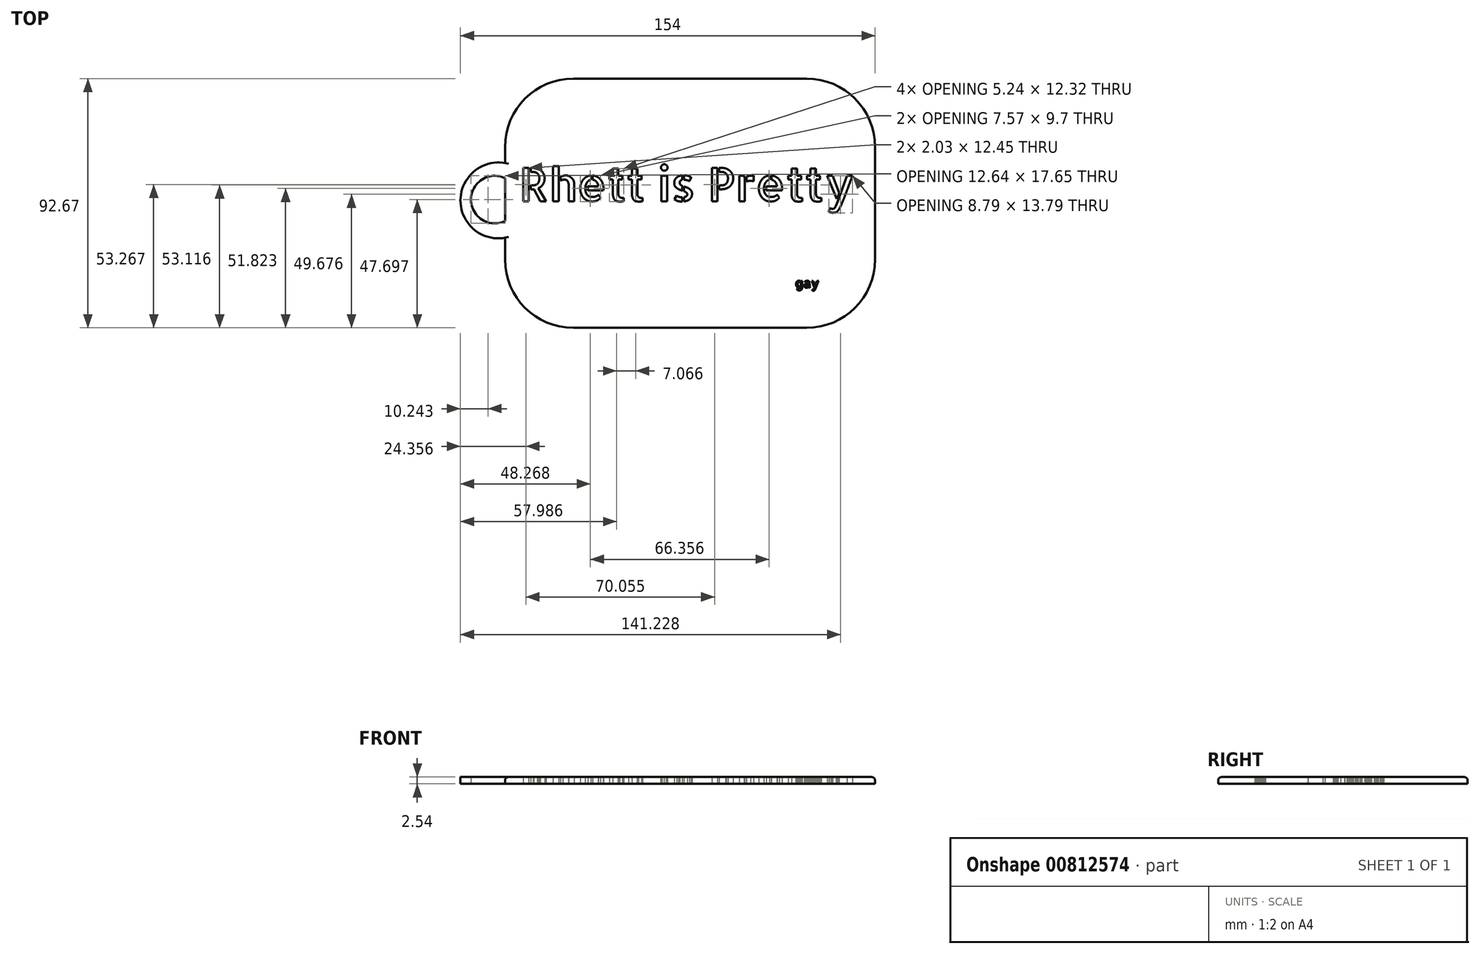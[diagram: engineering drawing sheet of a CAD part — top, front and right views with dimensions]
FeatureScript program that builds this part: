
annotation { "Feature Type Name" : "Feature", "Feature Type Description" : "" }
export const myFeature = defineFeature(function(context is Context, id is Id, definition is map)
    precondition{}
    {
        {
            var Q0;
            Q0=qCreatedBy(makeId("Top.planeOp"),FACE);
            var sketch = newSketch(context, id + "F0", { "sketchPlane" : qUnion([Q0])});
            skLineSegment(sketch, "E0.bottom", {"start": v(-64.83, 43.87) * mm, "end": v(72.61, 43.87) * mm});
            skLineSegment(sketch, "E0.top", {"start": v(-64.83, -48.8) * mm, "end": v(72.61, -48.8) * mm});
            skLineSegment(sketch, "E0.left", {"start": v(-64.83, 43.87) * mm, "end": v(-64.83, 12.46) * mm});
            skLineSegment(sketch, "E0.right", {"start": v(72.61, 43.87) * mm, "end": v(72.61, -48.8) * mm});
            skText(sketch, "E1", { "text": "Rhett is Pretty", "fontName": "AllertaStencil-Regular.ttf"});
            skText(sketch, "E2", { "text": "gay", "fontName": "AllertaStencil-Regular.ttf"});
            skArc(sketch, "E3", {"start": v(-64.83, 12.46) * mm, "mid": v(-81.4, -1.43) * mm, "end": v(-64.83, -15.31) * mm});
            skArc(sketch, "E4", {"start": v(-64.83, 6.88) * mm, "mid": v(-77.47, -1.1) * mm, "end": v(-64.83, -9.08) * mm});
            skLineSegment(sketch, "E5.trimOffspring", {"start": v(-64.83, -15.31) * mm, "end": v(-64.83, -48.8) * mm});
            skLineSegment(sketch, "E6", {"start": v(-64.83, 6.88) * mm, "end": v(-64.83, -9.08) * mm});
            const initialGuessF0  = {"E1": [-0.05957, -0.00176, 1, 0, 0.01246], "E2": [0.04298, -0.03385, 1, 0, 0.00333]};
            skSetInitialGuess(sketch, initialGuessF0);
            skSolve(sketch);
        }
        {
            var Q0;
            Q0=makeQuery(id+"F0.imprint","IMPRINT",FACE,{"disambiguationData":[TD([[makeQuery(id+"F0.imprint","IMPRINT",EDGE,{"derivedFrom":sQuery(id+"F0.wireOp",EDGE,"E0.bottom")}),-1.0]])]});
            extrude(context, id + "F1", {"entities" : qUnion([Q0]), "depth" : 2.54 * mm, "offsetDistance" : 25.4 * mm});
        }
        {
            var Q0;
            Q0=makeQuery(id+"F1.opExtrude","SWEPT_EDGE",EDGE,{"disambiguationData":[OSD([sQuery(id+"F0.wireOp",EDGE,"E0.bottom"),sQuery(id+"F0.wireOp",EDGE,"E0.left")])]});
            var Q1;
            Q1=makeQuery(id+"F1.opExtrude","SWEPT_EDGE",EDGE,{"disambiguationData":[OSD([sQuery(id+"F0.wireOp",EDGE,"E0.bottom"),sQuery(id+"F0.wireOp",EDGE,"E0.right")])]});
            var Q2;
            Q2=makeQuery(id+"F1.opExtrude","SWEPT_EDGE",EDGE,{"disambiguationData":[OSD([sQuery(id+"F0.wireOp",EDGE,"E0.top"),sQuery(id+"F0.wireOp",EDGE,"E0.right")])]});
            var Q3;
            Q3=makeQuery(id+"F1.opExtrude","SWEPT_EDGE",EDGE,{"disambiguationData":[OSD([sQuery(id+"F0.wireOp",EDGE,"E0.top"),sQuery(id+"F0.wireOp",EDGE,"E5.trimOffspring")])]});
            fillet(context, id + "F2", {"entities" : qUnion([Q0, Q1, Q2, Q3]), "radius" : 25.4 * mm, "tangentPropagation" : true, "allowEdgeOverflow" : false});
        }
        {
            var Q0;
            {var subQ0=sQuery(id+"F0.wireOp",EDGE,"E5.trimOffspring");var subQ1=sQuery(id+"F0.wireOp",EDGE,"E0.top");Q0=makeQuery(id+"F2.opFillet","BLEND_EDGE",EDGE,{"blendedFrom":[makeQuery(id+"F1.opExtrude","SWEPT_EDGE",EDGE,{"disambiguationData":[OSD([subQ1,subQ0])]}),makeQuery(id+"F1.opExtrude","CAP_FACE",FACE,{"disambiguationData":[OSD([sQuery(id+"F0.wireOp",EDGE,"E0.bottom"),subQ1,sQuery(id+"F0.wireOp",EDGE,"E0.left"),sQuery(id+"F0.wireOp",EDGE,"E0.right"),sQuery(id+"F0.wireOp",EDGE,"E1.sketch_text.stroke-0"),sQuery(id+"F0.wireOp",EDGE,"E1.sketch_text.stroke-1"),sQuery(id+"F0.wireOp",EDGE,"E1.sketch_text.stroke-2"),sQuery(id+"F0.wireOp",EDGE,"E1.sketch_text.stroke-3"),sQuery(id+"F0.wireOp",EDGE,"E1.sketch_text.stroke-4"),sQuery(id+"F0.wireOp",EDGE,"E1.sketch_text.stroke-5"),sQuery(id+"F0.wireOp",EDGE,"E1.sketch_text.stroke-6"),sQuery(id+"F0.wireOp",EDGE,"E1.sketch_text.stroke-7"),sQuery(id+"F0.wireOp",EDGE,"E1.sketch_text.stroke-8"),sQuery(id+"F0.wireOp",EDGE,"E1.sketch_text.stroke-9"),sQuery(id+"F0.wireOp",EDGE,"E1.sketch_text.stroke-10"),sQuery(id+"F0.wireOp",EDGE,"E1.sketch_text.stroke-11"),sQuery(id+"F0.wireOp",EDGE,"E1.sketch_text.stroke-12"),sQuery(id+"F0.wireOp",EDGE,"E1.sketch_text.stroke-13"),sQuery(id+"F0.wireOp",EDGE,"E1.sketch_text.stroke-14"),sQuery(id+"F0.wireOp",EDGE,"E1.sketch_text.stroke-15"),sQuery(id+"F0.wireOp",EDGE,"E1.sketch_text.stroke-16"),sQuery(id+"F0.wireOp",EDGE,"E1.sketch_text.stroke-17"),sQuery(id+"F0.wireOp",EDGE,"E1.sketch_text.stroke-18"),sQuery(id+"F0.wireOp",EDGE,"E1.sketch_text.stroke-19"),sQuery(id+"F0.wireOp",EDGE,"E1.sketch_text.stroke-20"),sQuery(id+"F0.wireOp",EDGE,"E1.sketch_text.stroke-21"),sQuery(id+"F0.wireOp",EDGE,"E1.sketch_text.stroke-22"),sQuery(id+"F0.wireOp",EDGE,"E1.sketch_text.stroke-23"),sQuery(id+"F0.wireOp",EDGE,"E1.sketch_text.stroke-24"),sQuery(id+"F0.wireOp",EDGE,"E1.sketch_text.stroke-25"),sQuery(id+"F0.wireOp",EDGE,"E1.sketch_text.stroke-26"),sQuery(id+"F0.wireOp",EDGE,"E1.sketch_text.stroke-27"),sQuery(id+"F0.wireOp",EDGE,"E1.sketch_text.stroke-28"),sQuery(id+"F0.wireOp",EDGE,"E1.sketch_text.stroke-29"),sQuery(id+"F0.wireOp",EDGE,"E1.sketch_text.stroke-30"),sQuery(id+"F0.wireOp",EDGE,"E1.sketch_text.stroke-31"),sQuery(id+"F0.wireOp",EDGE,"E1.sketch_text.stroke-32"),sQuery(id+"F0.wireOp",EDGE,"E1.sketch_text.stroke-33"),sQuery(id+"F0.wireOp",EDGE,"E1.sketch_text.stroke-34"),sQuery(id+"F0.wireOp",EDGE,"E1.sketch_text.stroke-35"),sQuery(id+"F0.wireOp",EDGE,"E1.sketch_text.stroke-36"),sQuery(id+"F0.wireOp",EDGE,"E1.sketch_text.stroke-37"),sQuery(id+"F0.wireOp",EDGE,"E1.sketch_text.stroke-38"),sQuery(id+"F0.wireOp",EDGE,"E1.sketch_text.stroke-39"),sQuery(id+"F0.wireOp",EDGE,"E1.sketch_text.stroke-40"),sQuery(id+"F0.wireOp",EDGE,"E1.sketch_text.stroke-41"),sQuery(id+"F0.wireOp",EDGE,"E1.sketch_text.stroke-42"),sQuery(id+"F0.wireOp",EDGE,"E1.sketch_text.stroke-43"),sQuery(id+"F0.wireOp",EDGE,"E1.sketch_text.stroke-44"),sQuery(id+"F0.wireOp",EDGE,"E1.sketch_text.stroke-45"),sQuery(id+"F0.wireOp",EDGE,"E1.sketch_text.stroke-46"),sQuery(id+"F0.wireOp",EDGE,"E1.sketch_text.stroke-47"),sQuery(id+"F0.wireOp",EDGE,"E1.sketch_text.stroke-48"),sQuery(id+"F0.wireOp",EDGE,"E1.sketch_text.stroke-49"),sQuery(id+"F0.wireOp",EDGE,"E1.sketch_text.stroke-50"),sQuery(id+"F0.wireOp",EDGE,"E1.sketch_text.stroke-51"),sQuery(id+"F0.wireOp",EDGE,"E1.sketch_text.stroke-52"),sQuery(id+"F0.wireOp",EDGE,"E1.sketch_text.stroke-53"),sQuery(id+"F0.wireOp",EDGE,"E1.sketch_text.stroke-54"),sQuery(id+"F0.wireOp",EDGE,"E1.sketch_text.stroke-55"),sQuery(id+"F0.wireOp",EDGE,"E1.sketch_text.stroke-56"),sQuery(id+"F0.wireOp",EDGE,"E1.sketch_text.stroke-57"),sQuery(id+"F0.wireOp",EDGE,"E1.sketch_text.stroke-58"),sQuery(id+"F0.wireOp",EDGE,"E1.sketch_text.stroke-59"),sQuery(id+"F0.wireOp",EDGE,"E1.sketch_text.stroke-60"),sQuery(id+"F0.wireOp",EDGE,"E1.sketch_text.stroke-61"),sQuery(id+"F0.wireOp",EDGE,"E1.sketch_text.stroke-62"),sQuery(id+"F0.wireOp",EDGE,"E1.sketch_text.stroke-63"),sQuery(id+"F0.wireOp",EDGE,"E1.sketch_text.stroke-64"),sQuery(id+"F0.wireOp",EDGE,"E1.sketch_text.stroke-65"),sQuery(id+"F0.wireOp",EDGE,"E1.sketch_text.stroke-66"),sQuery(id+"F0.wireOp",EDGE,"E1.sketch_text.stroke-67"),sQuery(id+"F0.wireOp",EDGE,"E1.sketch_text.stroke-68"),sQuery(id+"F0.wireOp",EDGE,"E1.sketch_text.stroke-69"),sQuery(id+"F0.wireOp",EDGE,"E1.sketch_text.stroke-70"),sQuery(id+"F0.wireOp",EDGE,"E1.sketch_text.stroke-71"),sQuery(id+"F0.wireOp",EDGE,"E1.sketch_text.stroke-72"),sQuery(id+"F0.wireOp",EDGE,"E1.sketch_text.stroke-73"),sQuery(id+"F0.wireOp",EDGE,"E1.sketch_text.stroke-74"),sQuery(id+"F0.wireOp",EDGE,"E1.sketch_text.stroke-75"),sQuery(id+"F0.wireOp",EDGE,"E1.sketch_text.stroke-76"),sQuery(id+"F0.wireOp",EDGE,"E1.sketch_text.stroke-77"),sQuery(id+"F0.wireOp",EDGE,"E1.sketch_text.stroke-78"),sQuery(id+"F0.wireOp",EDGE,"E1.sketch_text.stroke-79"),sQuery(id+"F0.wireOp",EDGE,"E1.sketch_text.stroke-80"),sQuery(id+"F0.wireOp",EDGE,"E1.sketch_text.stroke-81"),sQuery(id+"F0.wireOp",EDGE,"E1.sketch_text.stroke-82"),sQuery(id+"F0.wireOp",EDGE,"E1.sketch_text.stroke-83"),sQuery(id+"F0.wireOp",EDGE,"E1.sketch_text.stroke-84"),sQuery(id+"F0.wireOp",EDGE,"E1.sketch_text.stroke-85"),sQuery(id+"F0.wireOp",EDGE,"E1.sketch_text.stroke-86"),sQuery(id+"F0.wireOp",EDGE,"E1.sketch_text.stroke-87"),sQuery(id+"F0.wireOp",EDGE,"E1.sketch_text.stroke-88"),sQuery(id+"F0.wireOp",EDGE,"E1.sketch_text.stroke-89"),sQuery(id+"F0.wireOp",EDGE,"E1.sketch_text.stroke-90"),sQuery(id+"F0.wireOp",EDGE,"E1.sketch_text.stroke-91"),sQuery(id+"F0.wireOp",EDGE,"E1.sketch_text.stroke-92"),sQuery(id+"F0.wireOp",EDGE,"E1.sketch_text.stroke-93"),sQuery(id+"F0.wireOp",EDGE,"E1.sketch_text.stroke-94"),sQuery(id+"F0.wireOp",EDGE,"E1.sketch_text.stroke-95"),sQuery(id+"F0.wireOp",EDGE,"E1.sketch_text.stroke-96"),sQuery(id+"F0.wireOp",EDGE,"E1.sketch_text.stroke-97"),sQuery(id+"F0.wireOp",EDGE,"E1.sketch_text.stroke-98"),sQuery(id+"F0.wireOp",EDGE,"E1.sketch_text.stroke-99"),sQuery(id+"F0.wireOp",EDGE,"E1.sketch_text.stroke-100"),sQuery(id+"F0.wireOp",EDGE,"E1.sketch_text.stroke-101"),sQuery(id+"F0.wireOp",EDGE,"E1.sketch_text.stroke-102"),sQuery(id+"F0.wireOp",EDGE,"E1.sketch_text.stroke-103"),sQuery(id+"F0.wireOp",EDGE,"E1.sketch_text.stroke-104"),sQuery(id+"F0.wireOp",EDGE,"E1.sketch_text.stroke-105"),sQuery(id+"F0.wireOp",EDGE,"E1.sketch_text.stroke-106"),sQuery(id+"F0.wireOp",EDGE,"E1.sketch_text.stroke-107"),sQuery(id+"F0.wireOp",EDGE,"E1.sketch_text.stroke-108"),sQuery(id+"F0.wireOp",EDGE,"E1.sketch_text.stroke-109"),sQuery(id+"F0.wireOp",EDGE,"E1.sketch_text.stroke-110"),sQuery(id+"F0.wireOp",EDGE,"E1.sketch_text.stroke-111"),sQuery(id+"F0.wireOp",EDGE,"E1.sketch_text.stroke-112"),sQuery(id+"F0.wireOp",EDGE,"E1.sketch_text.stroke-113"),sQuery(id+"F0.wireOp",EDGE,"E1.sketch_text.stroke-114"),sQuery(id+"F0.wireOp",EDGE,"E1.sketch_text.stroke-115"),sQuery(id+"F0.wireOp",EDGE,"E1.sketch_text.stroke-116"),sQuery(id+"F0.wireOp",EDGE,"E1.sketch_text.stroke-117"),sQuery(id+"F0.wireOp",EDGE,"E1.sketch_text.stroke-118"),sQuery(id+"F0.wireOp",EDGE,"E1.sketch_text.stroke-119"),sQuery(id+"F0.wireOp",EDGE,"E1.sketch_text.stroke-120"),sQuery(id+"F0.wireOp",EDGE,"E1.sketch_text.stroke-121"),sQuery(id+"F0.wireOp",EDGE,"E1.sketch_text.stroke-122"),sQuery(id+"F0.wireOp",EDGE,"E1.sketch_text.stroke-123"),sQuery(id+"F0.wireOp",EDGE,"E1.sketch_text.stroke-124"),sQuery(id+"F0.wireOp",EDGE,"E1.sketch_text.stroke-125"),sQuery(id+"F0.wireOp",EDGE,"E1.sketch_text.stroke-126"),sQuery(id+"F0.wireOp",EDGE,"E1.sketch_text.stroke-127"),sQuery(id+"F0.wireOp",EDGE,"E1.sketch_text.stroke-128"),sQuery(id+"F0.wireOp",EDGE,"E1.sketch_text.stroke-129"),sQuery(id+"F0.wireOp",EDGE,"E1.sketch_text.stroke-130"),sQuery(id+"F0.wireOp",EDGE,"E1.sketch_text.stroke-131"),sQuery(id+"F0.wireOp",EDGE,"E1.sketch_text.stroke-132"),sQuery(id+"F0.wireOp",EDGE,"E1.sketch_text.stroke-133"),sQuery(id+"F0.wireOp",EDGE,"E1.sketch_text.stroke-134"),sQuery(id+"F0.wireOp",EDGE,"E1.sketch_text.stroke-135"),sQuery(id+"F0.wireOp",EDGE,"E1.sketch_text.stroke-136"),sQuery(id+"F0.wireOp",EDGE,"E1.sketch_text.stroke-137"),sQuery(id+"F0.wireOp",EDGE,"E1.sketch_text.stroke-138"),sQuery(id+"F0.wireOp",EDGE,"E1.sketch_text.stroke-139"),sQuery(id+"F0.wireOp",EDGE,"E1.sketch_text.stroke-140"),sQuery(id+"F0.wireOp",EDGE,"E1.sketch_text.stroke-141"),sQuery(id+"F0.wireOp",EDGE,"E1.sketch_text.stroke-142"),sQuery(id+"F0.wireOp",EDGE,"E1.sketch_text.stroke-143"),sQuery(id+"F0.wireOp",EDGE,"E1.sketch_text.stroke-144"),sQuery(id+"F0.wireOp",EDGE,"E1.sketch_text.stroke-145"),sQuery(id+"F0.wireOp",EDGE,"E1.sketch_text.stroke-146"),sQuery(id+"F0.wireOp",EDGE,"E1.sketch_text.stroke-147"),sQuery(id+"F0.wireOp",EDGE,"E1.sketch_text.stroke-148"),sQuery(id+"F0.wireOp",EDGE,"E1.sketch_text.stroke-149"),sQuery(id+"F0.wireOp",EDGE,"E1.sketch_text.stroke-150"),sQuery(id+"F0.wireOp",EDGE,"E1.sketch_text.stroke-151"),sQuery(id+"F0.wireOp",EDGE,"E1.sketch_text.stroke-152"),sQuery(id+"F0.wireOp",EDGE,"E1.sketch_text.stroke-153"),sQuery(id+"F0.wireOp",EDGE,"E1.sketch_text.stroke-154"),sQuery(id+"F0.wireOp",EDGE,"E1.sketch_text.stroke-155"),sQuery(id+"F0.wireOp",EDGE,"E1.sketch_text.stroke-156"),sQuery(id+"F0.wireOp",EDGE,"E1.sketch_text.stroke-157"),sQuery(id+"F0.wireOp",EDGE,"E1.sketch_text.stroke-158"),sQuery(id+"F0.wireOp",EDGE,"E1.sketch_text.stroke-159"),sQuery(id+"F0.wireOp",EDGE,"E1.sketch_text.stroke-160"),sQuery(id+"F0.wireOp",EDGE,"E1.sketch_text.stroke-161"),sQuery(id+"F0.wireOp",EDGE,"E1.sketch_text.stroke-162"),sQuery(id+"F0.wireOp",EDGE,"E1.sketch_text.stroke-163"),sQuery(id+"F0.wireOp",EDGE,"E1.sketch_text.stroke-164"),sQuery(id+"F0.wireOp",EDGE,"E1.sketch_text.stroke-165"),sQuery(id+"F0.wireOp",EDGE,"E1.sketch_text.stroke-166"),sQuery(id+"F0.wireOp",EDGE,"E1.sketch_text.stroke-167"),sQuery(id+"F0.wireOp",EDGE,"E1.sketch_text.stroke-168"),sQuery(id+"F0.wireOp",EDGE,"E1.sketch_text.stroke-169"),sQuery(id+"F0.wireOp",EDGE,"E1.sketch_text.stroke-170"),sQuery(id+"F0.wireOp",EDGE,"E1.sketch_text.stroke-171"),sQuery(id+"F0.wireOp",EDGE,"E1.sketch_text.stroke-172"),sQuery(id+"F0.wireOp",EDGE,"E1.sketch_text.stroke-173"),sQuery(id+"F0.wireOp",EDGE,"E1.sketch_text.stroke-174"),sQuery(id+"F0.wireOp",EDGE,"E1.sketch_text.stroke-175"),sQuery(id+"F0.wireOp",EDGE,"E1.sketch_text.stroke-176"),sQuery(id+"F0.wireOp",EDGE,"E1.sketch_text.stroke-177"),sQuery(id+"F0.wireOp",EDGE,"E1.sketch_text.stroke-178"),sQuery(id+"F0.wireOp",EDGE,"E1.sketch_text.stroke-179"),sQuery(id+"F0.wireOp",EDGE,"E1.sketch_text.stroke-180"),sQuery(id+"F0.wireOp",EDGE,"E1.sketch_text.stroke-181"),sQuery(id+"F0.wireOp",EDGE,"E1.sketch_text.stroke-182"),sQuery(id+"F0.wireOp",EDGE,"E1.sketch_text.stroke-183"),sQuery(id+"F0.wireOp",EDGE,"E1.sketch_text.stroke-184"),sQuery(id+"F0.wireOp",EDGE,"E1.sketch_text.stroke-185"),sQuery(id+"F0.wireOp",EDGE,"E1.sketch_text.stroke-186"),sQuery(id+"F0.wireOp",EDGE,"E1.sketch_text.stroke-187"),sQuery(id+"F0.wireOp",EDGE,"E1.sketch_text.stroke-188"),sQuery(id+"F0.wireOp",EDGE,"E1.sketch_text.stroke-189"),sQuery(id+"F0.wireOp",EDGE,"E1.sketch_text.stroke-190"),sQuery(id+"F0.wireOp",EDGE,"E1.sketch_text.stroke-191"),sQuery(id+"F0.wireOp",EDGE,"E1.sketch_text.stroke-192"),sQuery(id+"F0.wireOp",EDGE,"E1.sketch_text.stroke-193"),sQuery(id+"F0.wireOp",EDGE,"E1.sketch_text.stroke-194"),sQuery(id+"F0.wireOp",EDGE,"E1.sketch_text.stroke-195"),sQuery(id+"F0.wireOp",EDGE,"E1.sketch_text.stroke-196"),sQuery(id+"F0.wireOp",EDGE,"E1.sketch_text.stroke-197"),sQuery(id+"F0.wireOp",EDGE,"E1.sketch_text.stroke-198"),sQuery(id+"F0.wireOp",EDGE,"E1.sketch_text.stroke-199"),sQuery(id+"F0.wireOp",EDGE,"E1.sketch_text.stroke-200"),sQuery(id+"F0.wireOp",EDGE,"E1.sketch_text.stroke-201"),sQuery(id+"F0.wireOp",EDGE,"E1.sketch_text.stroke-202"),sQuery(id+"F0.wireOp",EDGE,"E1.sketch_text.stroke-203"),sQuery(id+"F0.wireOp",EDGE,"E1.sketch_text.stroke-204"),sQuery(id+"F0.wireOp",EDGE,"E1.sketch_text.stroke-205"),sQuery(id+"F0.wireOp",EDGE,"E1.sketch_text.stroke-206"),sQuery(id+"F0.wireOp",EDGE,"E1.sketch_text.stroke-207"),sQuery(id+"F0.wireOp",EDGE,"E1.sketch_text.stroke-208"),sQuery(id+"F0.wireOp",EDGE,"E1.sketch_text.stroke-209"),sQuery(id+"F0.wireOp",EDGE,"E1.sketch_text.stroke-210"),sQuery(id+"F0.wireOp",EDGE,"E1.sketch_text.stroke-211"),sQuery(id+"F0.wireOp",EDGE,"E1.sketch_text.stroke-212"),sQuery(id+"F0.wireOp",EDGE,"E1.sketch_text.stroke-213"),sQuery(id+"F0.wireOp",EDGE,"E1.sketch_text.stroke-214"),sQuery(id+"F0.wireOp",EDGE,"E1.sketch_text.stroke-215"),sQuery(id+"F0.wireOp",EDGE,"E1.sketch_text.stroke-216"),sQuery(id+"F0.wireOp",EDGE,"E1.sketch_text.stroke-217"),sQuery(id+"F0.wireOp",EDGE,"E1.sketch_text.stroke-218"),sQuery(id+"F0.wireOp",EDGE,"E1.sketch_text.stroke-219"),sQuery(id+"F0.wireOp",EDGE,"E1.sketch_text.stroke-220"),sQuery(id+"F0.wireOp",EDGE,"E1.sketch_text.stroke-221"),sQuery(id+"F0.wireOp",EDGE,"E1.sketch_text.stroke-222"),sQuery(id+"F0.wireOp",EDGE,"E1.sketch_text.stroke-223"),sQuery(id+"F0.wireOp",EDGE,"E1.sketch_text.stroke-224"),sQuery(id+"F0.wireOp",EDGE,"E1.sketch_text.stroke-225"),sQuery(id+"F0.wireOp",EDGE,"E1.sketch_text.stroke-226"),sQuery(id+"F0.wireOp",EDGE,"E1.sketch_text.stroke-227"),sQuery(id+"F0.wireOp",EDGE,"E1.sketch_text.stroke-228"),sQuery(id+"F0.wireOp",EDGE,"E1.sketch_text.stroke-229"),sQuery(id+"F0.wireOp",EDGE,"E1.sketch_text.stroke-230"),sQuery(id+"F0.wireOp",EDGE,"E1.sketch_text.stroke-231"),sQuery(id+"F0.wireOp",EDGE,"E1.sketch_text.stroke-232"),sQuery(id+"F0.wireOp",EDGE,"E1.sketch_text.stroke-233"),sQuery(id+"F0.wireOp",EDGE,"E1.sketch_text.stroke-234"),sQuery(id+"F0.wireOp",EDGE,"E1.sketch_text.stroke-235"),sQuery(id+"F0.wireOp",EDGE,"E1.sketch_text.stroke-236"),sQuery(id+"F0.wireOp",EDGE,"E1.sketch_text.stroke-237"),sQuery(id+"F0.wireOp",EDGE,"E1.sketch_text.stroke-238"),sQuery(id+"F0.wireOp",EDGE,"E1.sketch_text.stroke-239"),sQuery(id+"F0.wireOp",EDGE,"E1.sketch_text.stroke-240"),sQuery(id+"F0.wireOp",EDGE,"E1.sketch_text.stroke-241"),sQuery(id+"F0.wireOp",EDGE,"E1.sketch_text.stroke-242"),sQuery(id+"F0.wireOp",EDGE,"E1.sketch_text.stroke-243"),sQuery(id+"F0.wireOp",EDGE,"E1.sketch_text.stroke-244"),sQuery(id+"F0.wireOp",EDGE,"E1.sketch_text.stroke-245"),sQuery(id+"F0.wireOp",EDGE,"E1.sketch_text.stroke-246"),sQuery(id+"F0.wireOp",EDGE,"E1.sketch_text.stroke-247"),sQuery(id+"F0.wireOp",EDGE,"E1.sketch_text.stroke-248"),sQuery(id+"F0.wireOp",EDGE,"E1.sketch_text.stroke-249"),sQuery(id+"F0.wireOp",EDGE,"E1.sketch_text.stroke-250"),sQuery(id+"F0.wireOp",EDGE,"E1.sketch_text.stroke-251"),sQuery(id+"F0.wireOp",EDGE,"E1.sketch_text.stroke-252"),sQuery(id+"F0.wireOp",EDGE,"E1.sketch_text.stroke-253"),sQuery(id+"F0.wireOp",EDGE,"E1.sketch_text.stroke-254"),sQuery(id+"F0.wireOp",EDGE,"E1.sketch_text.stroke-255"),sQuery(id+"F0.wireOp",EDGE,"E1.sketch_text.stroke-256"),sQuery(id+"F0.wireOp",EDGE,"E1.sketch_text.stroke-257"),sQuery(id+"F0.wireOp",EDGE,"E1.sketch_text.stroke-258"),sQuery(id+"F0.wireOp",EDGE,"E1.sketch_text.stroke-259"),sQuery(id+"F0.wireOp",EDGE,"E1.sketch_text.stroke-260"),sQuery(id+"F0.wireOp",EDGE,"E1.sketch_text.stroke-261"),sQuery(id+"F0.wireOp",EDGE,"E1.sketch_text.stroke-262"),sQuery(id+"F0.wireOp",EDGE,"E1.sketch_text.stroke-263"),sQuery(id+"F0.wireOp",EDGE,"E1.sketch_text.stroke-264"),sQuery(id+"F0.wireOp",EDGE,"E1.sketch_text.stroke-265"),sQuery(id+"F0.wireOp",EDGE,"E1.sketch_text.stroke-266"),sQuery(id+"F0.wireOp",EDGE,"E1.sketch_text.stroke-267"),sQuery(id+"F0.wireOp",EDGE,"E1.sketch_text.stroke-268"),sQuery(id+"F0.wireOp",EDGE,"E1.sketch_text.stroke-269"),sQuery(id+"F0.wireOp",EDGE,"E1.sketch_text.stroke-270"),sQuery(id+"F0.wireOp",EDGE,"E1.sketch_text.stroke-271"),sQuery(id+"F0.wireOp",EDGE,"E1.sketch_text.stroke-272"),sQuery(id+"F0.wireOp",EDGE,"E1.sketch_text.stroke-273"),sQuery(id+"F0.wireOp",EDGE,"E1.sketch_text.stroke-274"),sQuery(id+"F0.wireOp",EDGE,"E1.sketch_text.stroke-275"),sQuery(id+"F0.wireOp",EDGE,"E1.sketch_text.stroke-276"),sQuery(id+"F0.wireOp",EDGE,"E1.sketch_text.stroke-277"),sQuery(id+"F0.wireOp",EDGE,"E1.sketch_text.stroke-278"),sQuery(id+"F0.wireOp",EDGE,"E1.sketch_text.stroke-279"),sQuery(id+"F0.wireOp",EDGE,"E1.sketch_text.stroke-280"),sQuery(id+"F0.wireOp",EDGE,"E1.sketch_text.stroke-281"),sQuery(id+"F0.wireOp",EDGE,"E1.sketch_text.stroke-282"),sQuery(id+"F0.wireOp",EDGE,"E1.sketch_text.stroke-283"),sQuery(id+"F0.wireOp",EDGE,"E1.sketch_text.stroke-284"),sQuery(id+"F0.wireOp",EDGE,"E1.sketch_text.stroke-285"),sQuery(id+"F0.wireOp",EDGE,"E1.sketch_text.stroke-286"),sQuery(id+"F0.wireOp",EDGE,"E1.sketch_text.stroke-287"),sQuery(id+"F0.wireOp",EDGE,"E1.sketch_text.stroke-288"),sQuery(id+"F0.wireOp",EDGE,"E1.sketch_text.stroke-289"),sQuery(id+"F0.wireOp",EDGE,"E1.sketch_text.stroke-290"),sQuery(id+"F0.wireOp",EDGE,"E1.sketch_text.stroke-291"),sQuery(id+"F0.wireOp",EDGE,"E1.sketch_text.stroke-292"),sQuery(id+"F0.wireOp",EDGE,"E1.sketch_text.stroke-293"),sQuery(id+"F0.wireOp",EDGE,"E1.sketch_text.stroke-294"),sQuery(id+"F0.wireOp",EDGE,"E1.sketch_text.stroke-295"),sQuery(id+"F0.wireOp",EDGE,"E1.sketch_text.stroke-296"),sQuery(id+"F0.wireOp",EDGE,"E1.sketch_text.stroke-297"),sQuery(id+"F0.wireOp",EDGE,"E1.sketch_text.stroke-298"),sQuery(id+"F0.wireOp",EDGE,"E1.sketch_text.stroke-299"),sQuery(id+"F0.wireOp",EDGE,"E1.sketch_text.stroke-300"),sQuery(id+"F0.wireOp",EDGE,"E1.sketch_text.stroke-301"),sQuery(id+"F0.wireOp",EDGE,"E1.sketch_text.stroke-302"),sQuery(id+"F0.wireOp",EDGE,"E1.sketch_text.stroke-303"),sQuery(id+"F0.wireOp",EDGE,"E1.sketch_text.stroke-304"),sQuery(id+"F0.wireOp",EDGE,"E1.sketch_text.stroke-305"),sQuery(id+"F0.wireOp",EDGE,"E1.sketch_text.stroke-306"),sQuery(id+"F0.wireOp",EDGE,"E1.sketch_text.stroke-307"),sQuery(id+"F0.wireOp",EDGE,"E1.sketch_text.stroke-308"),sQuery(id+"F0.wireOp",EDGE,"E1.sketch_text.stroke-309"),sQuery(id+"F0.wireOp",EDGE,"E1.sketch_text.stroke-310"),sQuery(id+"F0.wireOp",EDGE,"E1.sketch_text.stroke-311"),sQuery(id+"F0.wireOp",EDGE,"E1.sketch_text.stroke-312"),sQuery(id+"F0.wireOp",EDGE,"E1.sketch_text.stroke-313"),sQuery(id+"F0.wireOp",EDGE,"E1.sketch_text.stroke-314"),sQuery(id+"F0.wireOp",EDGE,"E1.sketch_text.stroke-315"),sQuery(id+"F0.wireOp",EDGE,"E1.sketch_text.stroke-316"),sQuery(id+"F0.wireOp",EDGE,"E1.sketch_text.stroke-317"),sQuery(id+"F0.wireOp",EDGE,"E1.sketch_text.stroke-318"),sQuery(id+"F0.wireOp",EDGE,"E1.sketch_text.stroke-319"),sQuery(id+"F0.wireOp",EDGE,"E1.sketch_text.stroke-320"),sQuery(id+"F0.wireOp",EDGE,"E1.sketch_text.stroke-321"),sQuery(id+"F0.wireOp",EDGE,"E1.sketch_text.stroke-322"),sQuery(id+"F0.wireOp",EDGE,"E1.sketch_text.stroke-323"),sQuery(id+"F0.wireOp",EDGE,"E1.sketch_text.stroke-324"),sQuery(id+"F0.wireOp",EDGE,"E1.sketch_text.stroke-325"),sQuery(id+"F0.wireOp",EDGE,"E1.sketch_text.stroke-326"),sQuery(id+"F0.wireOp",EDGE,"E1.sketch_text.stroke-327"),sQuery(id+"F0.wireOp",EDGE,"E1.sketch_text.stroke-328"),sQuery(id+"F0.wireOp",EDGE,"E1.sketch_text.stroke-329"),sQuery(id+"F0.wireOp",EDGE,"E1.sketch_text.stroke-330"),sQuery(id+"F0.wireOp",EDGE,"E1.sketch_text.stroke-331"),sQuery(id+"F0.wireOp",EDGE,"E1.sketch_text.stroke-332"),sQuery(id+"F0.wireOp",EDGE,"E1.sketch_text.stroke-333"),sQuery(id+"F0.wireOp",EDGE,"E1.sketch_text.stroke-334"),sQuery(id+"F0.wireOp",EDGE,"E1.sketch_text.stroke-335"),sQuery(id+"F0.wireOp",EDGE,"E1.sketch_text.stroke-336"),sQuery(id+"F0.wireOp",EDGE,"E1.sketch_text.stroke-337"),sQuery(id+"F0.wireOp",EDGE,"E1.sketch_text.stroke-338"),sQuery(id+"F0.wireOp",EDGE,"E1.sketch_text.stroke-339"),sQuery(id+"F0.wireOp",EDGE,"E1.sketch_text.stroke-340"),sQuery(id+"F0.wireOp",EDGE,"E1.sketch_text.stroke-341"),sQuery(id+"F0.wireOp",EDGE,"E1.sketch_text.stroke-342"),sQuery(id+"F0.wireOp",EDGE,"E1.sketch_text.stroke-343"),sQuery(id+"F0.wireOp",EDGE,"E1.sketch_text.stroke-344"),sQuery(id+"F0.wireOp",EDGE,"E1.sketch_text.stroke-345"),sQuery(id+"F0.wireOp",EDGE,"E1.sketch_text.stroke-346"),sQuery(id+"F0.wireOp",EDGE,"E1.sketch_text.stroke-347"),sQuery(id+"F0.wireOp",EDGE,"E1.sketch_text.stroke-348"),sQuery(id+"F0.wireOp",EDGE,"E1.sketch_text.stroke-349"),sQuery(id+"F0.wireOp",EDGE,"E1.sketch_text.stroke-350"),sQuery(id+"F0.wireOp",EDGE,"E2.sketch_text.stroke-0"),sQuery(id+"F0.wireOp",EDGE,"E2.sketch_text.stroke-1"),sQuery(id+"F0.wireOp",EDGE,"E2.sketch_text.stroke-2"),sQuery(id+"F0.wireOp",EDGE,"E2.sketch_text.stroke-3"),sQuery(id+"F0.wireOp",EDGE,"E2.sketch_text.stroke-4"),sQuery(id+"F0.wireOp",EDGE,"E2.sketch_text.stroke-5"),sQuery(id+"F0.wireOp",EDGE,"E2.sketch_text.stroke-6"),sQuery(id+"F0.wireOp",EDGE,"E2.sketch_text.stroke-7"),sQuery(id+"F0.wireOp",EDGE,"E2.sketch_text.stroke-8"),sQuery(id+"F0.wireOp",EDGE,"E2.sketch_text.stroke-9"),sQuery(id+"F0.wireOp",EDGE,"E2.sketch_text.stroke-10"),sQuery(id+"F0.wireOp",EDGE,"E2.sketch_text.stroke-11"),sQuery(id+"F0.wireOp",EDGE,"E2.sketch_text.stroke-12"),sQuery(id+"F0.wireOp",EDGE,"E2.sketch_text.stroke-13"),sQuery(id+"F0.wireOp",EDGE,"E2.sketch_text.stroke-14"),sQuery(id+"F0.wireOp",EDGE,"E2.sketch_text.stroke-15"),sQuery(id+"F0.wireOp",EDGE,"E2.sketch_text.stroke-16"),sQuery(id+"F0.wireOp",EDGE,"E2.sketch_text.stroke-17"),sQuery(id+"F0.wireOp",EDGE,"E2.sketch_text.stroke-18"),sQuery(id+"F0.wireOp",EDGE,"E2.sketch_text.stroke-19"),sQuery(id+"F0.wireOp",EDGE,"E2.sketch_text.stroke-20"),sQuery(id+"F0.wireOp",EDGE,"E2.sketch_text.stroke-21"),sQuery(id+"F0.wireOp",EDGE,"E2.sketch_text.stroke-22"),sQuery(id+"F0.wireOp",EDGE,"E2.sketch_text.stroke-23"),sQuery(id+"F0.wireOp",EDGE,"E2.sketch_text.stroke-24"),sQuery(id+"F0.wireOp",EDGE,"E2.sketch_text.stroke-25"),sQuery(id+"F0.wireOp",EDGE,"E2.sketch_text.stroke-26"),sQuery(id+"F0.wireOp",EDGE,"E2.sketch_text.stroke-27"),sQuery(id+"F0.wireOp",EDGE,"E2.sketch_text.stroke-28"),sQuery(id+"F0.wireOp",EDGE,"E2.sketch_text.stroke-29"),sQuery(id+"F0.wireOp",EDGE,"E2.sketch_text.stroke-30"),sQuery(id+"F0.wireOp",EDGE,"E2.sketch_text.stroke-31"),sQuery(id+"F0.wireOp",EDGE,"E2.sketch_text.stroke-32"),sQuery(id+"F0.wireOp",EDGE,"E2.sketch_text.stroke-33"),sQuery(id+"F0.wireOp",EDGE,"E2.sketch_text.stroke-34"),sQuery(id+"F0.wireOp",EDGE,"E2.sketch_text.stroke-35"),sQuery(id+"F0.wireOp",EDGE,"E2.sketch_text.stroke-36"),sQuery(id+"F0.wireOp",EDGE,"E2.sketch_text.stroke-37"),sQuery(id+"F0.wireOp",EDGE,"E2.sketch_text.stroke-38"),sQuery(id+"F0.wireOp",EDGE,"E2.sketch_text.stroke-39"),sQuery(id+"F0.wireOp",EDGE,"E2.sketch_text.stroke-40"),sQuery(id+"F0.wireOp",EDGE,"E2.sketch_text.stroke-41"),sQuery(id+"F0.wireOp",EDGE,"E2.sketch_text.stroke-42"),sQuery(id+"F0.wireOp",EDGE,"E2.sketch_text.stroke-43"),sQuery(id+"F0.wireOp",EDGE,"E2.sketch_text.stroke-44"),sQuery(id+"F0.wireOp",EDGE,"E2.sketch_text.stroke-45"),sQuery(id+"F0.wireOp",EDGE,"E2.sketch_text.stroke-46"),sQuery(id+"F0.wireOp",EDGE,"E2.sketch_text.stroke-47"),sQuery(id+"F0.wireOp",EDGE,"E2.sketch_text.stroke-48"),sQuery(id+"F0.wireOp",EDGE,"E2.sketch_text.stroke-49"),sQuery(id+"F0.wireOp",EDGE,"E2.sketch_text.stroke-50"),sQuery(id+"F0.wireOp",EDGE,"E2.sketch_text.stroke-51"),sQuery(id+"F0.wireOp",EDGE,"E2.sketch_text.stroke-52"),sQuery(id+"F0.wireOp",EDGE,"E2.sketch_text.stroke-53"),sQuery(id+"F0.wireOp",EDGE,"E2.sketch_text.stroke-54"),sQuery(id+"F0.wireOp",EDGE,"E2.sketch_text.stroke-55"),sQuery(id+"F0.wireOp",EDGE,"E2.sketch_text.stroke-56"),sQuery(id+"F0.wireOp",EDGE,"E2.sketch_text.stroke-57"),sQuery(id+"F0.wireOp",EDGE,"E2.sketch_text.stroke-58"),sQuery(id+"F0.wireOp",EDGE,"E2.sketch_text.stroke-59"),sQuery(id+"F0.wireOp",EDGE,"E2.sketch_text.stroke-60"),sQuery(id+"F0.wireOp",EDGE,"E2.sketch_text.stroke-61"),sQuery(id+"F0.wireOp",EDGE,"E2.sketch_text.stroke-62"),sQuery(id+"F0.wireOp",EDGE,"E2.sketch_text.stroke-63"),sQuery(id+"F0.wireOp",EDGE,"E2.sketch_text.stroke-64"),sQuery(id+"F0.wireOp",EDGE,"E2.sketch_text.stroke-65"),sQuery(id+"F0.wireOp",EDGE,"E2.sketch_text.stroke-66"),sQuery(id+"F0.wireOp",EDGE,"E2.sketch_text.stroke-67"),sQuery(id+"F0.wireOp",EDGE,"E2.sketch_text.stroke-68"),sQuery(id+"F0.wireOp",EDGE,"E2.sketch_text.stroke-69"),sQuery(id+"F0.wireOp",EDGE,"E2.sketch_text.stroke-70"),sQuery(id+"F0.wireOp",EDGE,"E2.sketch_text.stroke-71"),sQuery(id+"F0.wireOp",EDGE,"E2.sketch_text.stroke-72"),sQuery(id+"F0.wireOp",EDGE,"E2.sketch_text.stroke-73"),sQuery(id+"F0.wireOp",EDGE,"E2.sketch_text.stroke-74"),sQuery(id+"F0.wireOp",EDGE,"E2.sketch_text.stroke-75"),sQuery(id+"F0.wireOp",EDGE,"E2.sketch_text.stroke-76"),sQuery(id+"F0.wireOp",EDGE,"E2.sketch_text.stroke-77"),sQuery(id+"F0.wireOp",EDGE,"E2.sketch_text.stroke-78"),sQuery(id+"F0.wireOp",EDGE,"E2.sketch_text.stroke-79"),sQuery(id+"F0.wireOp",EDGE,"E2.sketch_text.stroke-80"),sQuery(id+"F0.wireOp",EDGE,"E2.sketch_text.stroke-81"),sQuery(id+"F0.wireOp",EDGE,"E2.sketch_text.stroke-82"),sQuery(id+"F0.wireOp",EDGE,"E2.sketch_text.stroke-83"),sQuery(id+"F0.wireOp",EDGE,"E2.sketch_text.stroke-84"),sQuery(id+"F0.wireOp",EDGE,"E2.sketch_text.stroke-85"),sQuery(id+"F0.wireOp",EDGE,"E2.sketch_text.stroke-86"),sQuery(id+"F0.wireOp",EDGE,"E2.sketch_text.stroke-87"),sQuery(id+"F0.wireOp",EDGE,"E2.sketch_text.stroke-88"),sQuery(id+"F0.wireOp",EDGE,"E2.sketch_text.stroke-89"),sQuery(id+"F0.wireOp",EDGE,"E2.sketch_text.stroke-90"),sQuery(id+"F0.wireOp",EDGE,"E2.sketch_text.stroke-91"),sQuery(id+"F0.wireOp",EDGE,"E2.sketch_text.stroke-92"),sQuery(id+"F0.wireOp",EDGE,"E2.sketch_text.stroke-93"),sQuery(id+"F0.wireOp",EDGE,"E2.sketch_text.stroke-94"),sQuery(id+"F0.wireOp",EDGE,"E2.sketch_text.stroke-95"),sQuery(id+"F0.wireOp",EDGE,"E2.sketch_text.stroke-96"),sQuery(id+"F0.wireOp",EDGE,"E2.sketch_text.stroke-97"),sQuery(id+"F0.wireOp",EDGE,"E2.sketch_text.stroke-98"),sQuery(id+"F0.wireOp",EDGE,"E2.sketch_text.stroke-99"),sQuery(id+"F0.wireOp",EDGE,"E2.sketch_text.stroke-100"),sQuery(id+"F0.wireOp",EDGE,"E2.sketch_text.stroke-101"),sQuery(id+"F0.wireOp",EDGE,"E2.sketch_text.stroke-102"),sQuery(id+"F0.wireOp",EDGE,"E2.sketch_text.stroke-103"),sQuery(id+"F0.wireOp",EDGE,"E2.sketch_text.stroke-104"),sQuery(id+"F0.wireOp",EDGE,"E2.sketch_text.stroke-105"),sQuery(id+"F0.wireOp",EDGE,"E2.sketch_text.stroke-106"),sQuery(id+"F0.wireOp",EDGE,"E2.sketch_text.stroke-107"),sQuery(id+"F0.wireOp",EDGE,"E2.sketch_text.stroke-108"),sQuery(id+"F0.wireOp",EDGE,"E2.sketch_text.stroke-109"),sQuery(id+"F0.wireOp",EDGE,"E2.sketch_text.stroke-110"),sQuery(id+"F0.wireOp",EDGE,"E2.sketch_text.stroke-111"),sQuery(id+"F0.wireOp",EDGE,"E2.sketch_text.stroke-112"),sQuery(id+"F0.wireOp",EDGE,"E2.sketch_text.stroke-113"),sQuery(id+"F0.wireOp",EDGE,"E2.sketch_text.stroke-114"),sQuery(id+"F0.wireOp",EDGE,"E2.sketch_text.stroke-115"),sQuery(id+"F0.wireOp",EDGE,"E2.sketch_text.stroke-116"),sQuery(id+"F0.wireOp",EDGE,"E2.sketch_text.stroke-117"),sQuery(id+"F0.wireOp",EDGE,"E2.sketch_text.stroke-118"),sQuery(id+"F0.wireOp",EDGE,"E2.sketch_text.stroke-119"),sQuery(id+"F0.wireOp",EDGE,"E2.sketch_text.stroke-120"),sQuery(id+"F0.wireOp",EDGE,"E2.sketch_text.stroke-121"),sQuery(id+"F0.wireOp",EDGE,"E2.sketch_text.stroke-122"),sQuery(id+"F0.wireOp",EDGE,"E2.sketch_text.stroke-123"),sQuery(id+"F0.wireOp",EDGE,"E2.sketch_text.stroke-124"),sQuery(id+"F0.wireOp",EDGE,"E2.sketch_text.stroke-125"),sQuery(id+"F0.wireOp",EDGE,"E2.sketch_text.stroke-126"),sQuery(id+"F0.wireOp",EDGE,"E3"),sQuery(id+"F0.wireOp",EDGE,"E4"),subQ0,sQuery(id+"F0.wireOp",EDGE,"E6")])],"isStart":false})],"blendedInto":[makeQuery(id+"F1.opExtrude","CAP_FACE",FACE,{"disambiguationData":[OSD([sQuery(id+"F0.wireOp",EDGE,"E0.bottom"),subQ1,sQuery(id+"F0.wireOp",EDGE,"E0.left"),sQuery(id+"F0.wireOp",EDGE,"E0.right"),sQuery(id+"F0.wireOp",EDGE,"E1.sketch_text.stroke-0"),sQuery(id+"F0.wireOp",EDGE,"E1.sketch_text.stroke-1"),sQuery(id+"F0.wireOp",EDGE,"E1.sketch_text.stroke-2"),sQuery(id+"F0.wireOp",EDGE,"E1.sketch_text.stroke-3"),sQuery(id+"F0.wireOp",EDGE,"E1.sketch_text.stroke-4"),sQuery(id+"F0.wireOp",EDGE,"E1.sketch_text.stroke-5"),sQuery(id+"F0.wireOp",EDGE,"E1.sketch_text.stroke-6"),sQuery(id+"F0.wireOp",EDGE,"E1.sketch_text.stroke-7"),sQuery(id+"F0.wireOp",EDGE,"E1.sketch_text.stroke-8"),sQuery(id+"F0.wireOp",EDGE,"E1.sketch_text.stroke-9"),sQuery(id+"F0.wireOp",EDGE,"E1.sketch_text.stroke-10"),sQuery(id+"F0.wireOp",EDGE,"E1.sketch_text.stroke-11"),sQuery(id+"F0.wireOp",EDGE,"E1.sketch_text.stroke-12"),sQuery(id+"F0.wireOp",EDGE,"E1.sketch_text.stroke-13"),sQuery(id+"F0.wireOp",EDGE,"E1.sketch_text.stroke-14"),sQuery(id+"F0.wireOp",EDGE,"E1.sketch_text.stroke-15"),sQuery(id+"F0.wireOp",EDGE,"E1.sketch_text.stroke-16"),sQuery(id+"F0.wireOp",EDGE,"E1.sketch_text.stroke-17"),sQuery(id+"F0.wireOp",EDGE,"E1.sketch_text.stroke-18"),sQuery(id+"F0.wireOp",EDGE,"E1.sketch_text.stroke-19"),sQuery(id+"F0.wireOp",EDGE,"E1.sketch_text.stroke-20"),sQuery(id+"F0.wireOp",EDGE,"E1.sketch_text.stroke-21"),sQuery(id+"F0.wireOp",EDGE,"E1.sketch_text.stroke-22"),sQuery(id+"F0.wireOp",EDGE,"E1.sketch_text.stroke-23"),sQuery(id+"F0.wireOp",EDGE,"E1.sketch_text.stroke-24"),sQuery(id+"F0.wireOp",EDGE,"E1.sketch_text.stroke-25"),sQuery(id+"F0.wireOp",EDGE,"E1.sketch_text.stroke-26"),sQuery(id+"F0.wireOp",EDGE,"E1.sketch_text.stroke-27"),sQuery(id+"F0.wireOp",EDGE,"E1.sketch_text.stroke-28"),sQuery(id+"F0.wireOp",EDGE,"E1.sketch_text.stroke-29"),sQuery(id+"F0.wireOp",EDGE,"E1.sketch_text.stroke-30"),sQuery(id+"F0.wireOp",EDGE,"E1.sketch_text.stroke-31"),sQuery(id+"F0.wireOp",EDGE,"E1.sketch_text.stroke-32"),sQuery(id+"F0.wireOp",EDGE,"E1.sketch_text.stroke-33"),sQuery(id+"F0.wireOp",EDGE,"E1.sketch_text.stroke-34"),sQuery(id+"F0.wireOp",EDGE,"E1.sketch_text.stroke-35"),sQuery(id+"F0.wireOp",EDGE,"E1.sketch_text.stroke-36"),sQuery(id+"F0.wireOp",EDGE,"E1.sketch_text.stroke-37"),sQuery(id+"F0.wireOp",EDGE,"E1.sketch_text.stroke-38"),sQuery(id+"F0.wireOp",EDGE,"E1.sketch_text.stroke-39"),sQuery(id+"F0.wireOp",EDGE,"E1.sketch_text.stroke-40"),sQuery(id+"F0.wireOp",EDGE,"E1.sketch_text.stroke-41"),sQuery(id+"F0.wireOp",EDGE,"E1.sketch_text.stroke-42"),sQuery(id+"F0.wireOp",EDGE,"E1.sketch_text.stroke-43"),sQuery(id+"F0.wireOp",EDGE,"E1.sketch_text.stroke-44"),sQuery(id+"F0.wireOp",EDGE,"E1.sketch_text.stroke-45"),sQuery(id+"F0.wireOp",EDGE,"E1.sketch_text.stroke-46"),sQuery(id+"F0.wireOp",EDGE,"E1.sketch_text.stroke-47"),sQuery(id+"F0.wireOp",EDGE,"E1.sketch_text.stroke-48"),sQuery(id+"F0.wireOp",EDGE,"E1.sketch_text.stroke-49"),sQuery(id+"F0.wireOp",EDGE,"E1.sketch_text.stroke-50"),sQuery(id+"F0.wireOp",EDGE,"E1.sketch_text.stroke-51"),sQuery(id+"F0.wireOp",EDGE,"E1.sketch_text.stroke-52"),sQuery(id+"F0.wireOp",EDGE,"E1.sketch_text.stroke-53"),sQuery(id+"F0.wireOp",EDGE,"E1.sketch_text.stroke-54"),sQuery(id+"F0.wireOp",EDGE,"E1.sketch_text.stroke-55"),sQuery(id+"F0.wireOp",EDGE,"E1.sketch_text.stroke-56"),sQuery(id+"F0.wireOp",EDGE,"E1.sketch_text.stroke-57"),sQuery(id+"F0.wireOp",EDGE,"E1.sketch_text.stroke-58"),sQuery(id+"F0.wireOp",EDGE,"E1.sketch_text.stroke-59"),sQuery(id+"F0.wireOp",EDGE,"E1.sketch_text.stroke-60"),sQuery(id+"F0.wireOp",EDGE,"E1.sketch_text.stroke-61"),sQuery(id+"F0.wireOp",EDGE,"E1.sketch_text.stroke-62"),sQuery(id+"F0.wireOp",EDGE,"E1.sketch_text.stroke-63"),sQuery(id+"F0.wireOp",EDGE,"E1.sketch_text.stroke-64"),sQuery(id+"F0.wireOp",EDGE,"E1.sketch_text.stroke-65"),sQuery(id+"F0.wireOp",EDGE,"E1.sketch_text.stroke-66"),sQuery(id+"F0.wireOp",EDGE,"E1.sketch_text.stroke-67"),sQuery(id+"F0.wireOp",EDGE,"E1.sketch_text.stroke-68"),sQuery(id+"F0.wireOp",EDGE,"E1.sketch_text.stroke-69"),sQuery(id+"F0.wireOp",EDGE,"E1.sketch_text.stroke-70"),sQuery(id+"F0.wireOp",EDGE,"E1.sketch_text.stroke-71"),sQuery(id+"F0.wireOp",EDGE,"E1.sketch_text.stroke-72"),sQuery(id+"F0.wireOp",EDGE,"E1.sketch_text.stroke-73"),sQuery(id+"F0.wireOp",EDGE,"E1.sketch_text.stroke-74"),sQuery(id+"F0.wireOp",EDGE,"E1.sketch_text.stroke-75"),sQuery(id+"F0.wireOp",EDGE,"E1.sketch_text.stroke-76"),sQuery(id+"F0.wireOp",EDGE,"E1.sketch_text.stroke-77"),sQuery(id+"F0.wireOp",EDGE,"E1.sketch_text.stroke-78"),sQuery(id+"F0.wireOp",EDGE,"E1.sketch_text.stroke-79"),sQuery(id+"F0.wireOp",EDGE,"E1.sketch_text.stroke-80"),sQuery(id+"F0.wireOp",EDGE,"E1.sketch_text.stroke-81"),sQuery(id+"F0.wireOp",EDGE,"E1.sketch_text.stroke-82"),sQuery(id+"F0.wireOp",EDGE,"E1.sketch_text.stroke-83"),sQuery(id+"F0.wireOp",EDGE,"E1.sketch_text.stroke-84"),sQuery(id+"F0.wireOp",EDGE,"E1.sketch_text.stroke-85"),sQuery(id+"F0.wireOp",EDGE,"E1.sketch_text.stroke-86"),sQuery(id+"F0.wireOp",EDGE,"E1.sketch_text.stroke-87"),sQuery(id+"F0.wireOp",EDGE,"E1.sketch_text.stroke-88"),sQuery(id+"F0.wireOp",EDGE,"E1.sketch_text.stroke-89"),sQuery(id+"F0.wireOp",EDGE,"E1.sketch_text.stroke-90"),sQuery(id+"F0.wireOp",EDGE,"E1.sketch_text.stroke-91"),sQuery(id+"F0.wireOp",EDGE,"E1.sketch_text.stroke-92"),sQuery(id+"F0.wireOp",EDGE,"E1.sketch_text.stroke-93"),sQuery(id+"F0.wireOp",EDGE,"E1.sketch_text.stroke-94"),sQuery(id+"F0.wireOp",EDGE,"E1.sketch_text.stroke-95"),sQuery(id+"F0.wireOp",EDGE,"E1.sketch_text.stroke-96"),sQuery(id+"F0.wireOp",EDGE,"E1.sketch_text.stroke-97"),sQuery(id+"F0.wireOp",EDGE,"E1.sketch_text.stroke-98"),sQuery(id+"F0.wireOp",EDGE,"E1.sketch_text.stroke-99"),sQuery(id+"F0.wireOp",EDGE,"E1.sketch_text.stroke-100"),sQuery(id+"F0.wireOp",EDGE,"E1.sketch_text.stroke-101"),sQuery(id+"F0.wireOp",EDGE,"E1.sketch_text.stroke-102"),sQuery(id+"F0.wireOp",EDGE,"E1.sketch_text.stroke-103"),sQuery(id+"F0.wireOp",EDGE,"E1.sketch_text.stroke-104"),sQuery(id+"F0.wireOp",EDGE,"E1.sketch_text.stroke-105"),sQuery(id+"F0.wireOp",EDGE,"E1.sketch_text.stroke-106"),sQuery(id+"F0.wireOp",EDGE,"E1.sketch_text.stroke-107"),sQuery(id+"F0.wireOp",EDGE,"E1.sketch_text.stroke-108"),sQuery(id+"F0.wireOp",EDGE,"E1.sketch_text.stroke-109"),sQuery(id+"F0.wireOp",EDGE,"E1.sketch_text.stroke-110"),sQuery(id+"F0.wireOp",EDGE,"E1.sketch_text.stroke-111"),sQuery(id+"F0.wireOp",EDGE,"E1.sketch_text.stroke-112"),sQuery(id+"F0.wireOp",EDGE,"E1.sketch_text.stroke-113"),sQuery(id+"F0.wireOp",EDGE,"E1.sketch_text.stroke-114"),sQuery(id+"F0.wireOp",EDGE,"E1.sketch_text.stroke-115"),sQuery(id+"F0.wireOp",EDGE,"E1.sketch_text.stroke-116"),sQuery(id+"F0.wireOp",EDGE,"E1.sketch_text.stroke-117"),sQuery(id+"F0.wireOp",EDGE,"E1.sketch_text.stroke-118"),sQuery(id+"F0.wireOp",EDGE,"E1.sketch_text.stroke-119"),sQuery(id+"F0.wireOp",EDGE,"E1.sketch_text.stroke-120"),sQuery(id+"F0.wireOp",EDGE,"E1.sketch_text.stroke-121"),sQuery(id+"F0.wireOp",EDGE,"E1.sketch_text.stroke-122"),sQuery(id+"F0.wireOp",EDGE,"E1.sketch_text.stroke-123"),sQuery(id+"F0.wireOp",EDGE,"E1.sketch_text.stroke-124"),sQuery(id+"F0.wireOp",EDGE,"E1.sketch_text.stroke-125"),sQuery(id+"F0.wireOp",EDGE,"E1.sketch_text.stroke-126"),sQuery(id+"F0.wireOp",EDGE,"E1.sketch_text.stroke-127"),sQuery(id+"F0.wireOp",EDGE,"E1.sketch_text.stroke-128"),sQuery(id+"F0.wireOp",EDGE,"E1.sketch_text.stroke-129"),sQuery(id+"F0.wireOp",EDGE,"E1.sketch_text.stroke-130"),sQuery(id+"F0.wireOp",EDGE,"E1.sketch_text.stroke-131"),sQuery(id+"F0.wireOp",EDGE,"E1.sketch_text.stroke-132"),sQuery(id+"F0.wireOp",EDGE,"E1.sketch_text.stroke-133"),sQuery(id+"F0.wireOp",EDGE,"E1.sketch_text.stroke-134"),sQuery(id+"F0.wireOp",EDGE,"E1.sketch_text.stroke-135"),sQuery(id+"F0.wireOp",EDGE,"E1.sketch_text.stroke-136"),sQuery(id+"F0.wireOp",EDGE,"E1.sketch_text.stroke-137"),sQuery(id+"F0.wireOp",EDGE,"E1.sketch_text.stroke-138"),sQuery(id+"F0.wireOp",EDGE,"E1.sketch_text.stroke-139"),sQuery(id+"F0.wireOp",EDGE,"E1.sketch_text.stroke-140"),sQuery(id+"F0.wireOp",EDGE,"E1.sketch_text.stroke-141"),sQuery(id+"F0.wireOp",EDGE,"E1.sketch_text.stroke-142"),sQuery(id+"F0.wireOp",EDGE,"E1.sketch_text.stroke-143"),sQuery(id+"F0.wireOp",EDGE,"E1.sketch_text.stroke-144"),sQuery(id+"F0.wireOp",EDGE,"E1.sketch_text.stroke-145"),sQuery(id+"F0.wireOp",EDGE,"E1.sketch_text.stroke-146"),sQuery(id+"F0.wireOp",EDGE,"E1.sketch_text.stroke-147"),sQuery(id+"F0.wireOp",EDGE,"E1.sketch_text.stroke-148"),sQuery(id+"F0.wireOp",EDGE,"E1.sketch_text.stroke-149"),sQuery(id+"F0.wireOp",EDGE,"E1.sketch_text.stroke-150"),sQuery(id+"F0.wireOp",EDGE,"E1.sketch_text.stroke-151"),sQuery(id+"F0.wireOp",EDGE,"E1.sketch_text.stroke-152"),sQuery(id+"F0.wireOp",EDGE,"E1.sketch_text.stroke-153"),sQuery(id+"F0.wireOp",EDGE,"E1.sketch_text.stroke-154"),sQuery(id+"F0.wireOp",EDGE,"E1.sketch_text.stroke-155"),sQuery(id+"F0.wireOp",EDGE,"E1.sketch_text.stroke-156"),sQuery(id+"F0.wireOp",EDGE,"E1.sketch_text.stroke-157"),sQuery(id+"F0.wireOp",EDGE,"E1.sketch_text.stroke-158"),sQuery(id+"F0.wireOp",EDGE,"E1.sketch_text.stroke-159"),sQuery(id+"F0.wireOp",EDGE,"E1.sketch_text.stroke-160"),sQuery(id+"F0.wireOp",EDGE,"E1.sketch_text.stroke-161"),sQuery(id+"F0.wireOp",EDGE,"E1.sketch_text.stroke-162"),sQuery(id+"F0.wireOp",EDGE,"E1.sketch_text.stroke-163"),sQuery(id+"F0.wireOp",EDGE,"E1.sketch_text.stroke-164"),sQuery(id+"F0.wireOp",EDGE,"E1.sketch_text.stroke-165"),sQuery(id+"F0.wireOp",EDGE,"E1.sketch_text.stroke-166"),sQuery(id+"F0.wireOp",EDGE,"E1.sketch_text.stroke-167"),sQuery(id+"F0.wireOp",EDGE,"E1.sketch_text.stroke-168"),sQuery(id+"F0.wireOp",EDGE,"E1.sketch_text.stroke-169"),sQuery(id+"F0.wireOp",EDGE,"E1.sketch_text.stroke-170"),sQuery(id+"F0.wireOp",EDGE,"E1.sketch_text.stroke-171"),sQuery(id+"F0.wireOp",EDGE,"E1.sketch_text.stroke-172"),sQuery(id+"F0.wireOp",EDGE,"E1.sketch_text.stroke-173"),sQuery(id+"F0.wireOp",EDGE,"E1.sketch_text.stroke-174"),sQuery(id+"F0.wireOp",EDGE,"E1.sketch_text.stroke-175"),sQuery(id+"F0.wireOp",EDGE,"E1.sketch_text.stroke-176"),sQuery(id+"F0.wireOp",EDGE,"E1.sketch_text.stroke-177"),sQuery(id+"F0.wireOp",EDGE,"E1.sketch_text.stroke-178"),sQuery(id+"F0.wireOp",EDGE,"E1.sketch_text.stroke-179"),sQuery(id+"F0.wireOp",EDGE,"E1.sketch_text.stroke-180"),sQuery(id+"F0.wireOp",EDGE,"E1.sketch_text.stroke-181"),sQuery(id+"F0.wireOp",EDGE,"E1.sketch_text.stroke-182"),sQuery(id+"F0.wireOp",EDGE,"E1.sketch_text.stroke-183"),sQuery(id+"F0.wireOp",EDGE,"E1.sketch_text.stroke-184"),sQuery(id+"F0.wireOp",EDGE,"E1.sketch_text.stroke-185"),sQuery(id+"F0.wireOp",EDGE,"E1.sketch_text.stroke-186"),sQuery(id+"F0.wireOp",EDGE,"E1.sketch_text.stroke-187"),sQuery(id+"F0.wireOp",EDGE,"E1.sketch_text.stroke-188"),sQuery(id+"F0.wireOp",EDGE,"E1.sketch_text.stroke-189"),sQuery(id+"F0.wireOp",EDGE,"E1.sketch_text.stroke-190"),sQuery(id+"F0.wireOp",EDGE,"E1.sketch_text.stroke-191"),sQuery(id+"F0.wireOp",EDGE,"E1.sketch_text.stroke-192"),sQuery(id+"F0.wireOp",EDGE,"E1.sketch_text.stroke-193"),sQuery(id+"F0.wireOp",EDGE,"E1.sketch_text.stroke-194"),sQuery(id+"F0.wireOp",EDGE,"E1.sketch_text.stroke-195"),sQuery(id+"F0.wireOp",EDGE,"E1.sketch_text.stroke-196"),sQuery(id+"F0.wireOp",EDGE,"E1.sketch_text.stroke-197"),sQuery(id+"F0.wireOp",EDGE,"E1.sketch_text.stroke-198"),sQuery(id+"F0.wireOp",EDGE,"E1.sketch_text.stroke-199"),sQuery(id+"F0.wireOp",EDGE,"E1.sketch_text.stroke-200"),sQuery(id+"F0.wireOp",EDGE,"E1.sketch_text.stroke-201"),sQuery(id+"F0.wireOp",EDGE,"E1.sketch_text.stroke-202"),sQuery(id+"F0.wireOp",EDGE,"E1.sketch_text.stroke-203"),sQuery(id+"F0.wireOp",EDGE,"E1.sketch_text.stroke-204"),sQuery(id+"F0.wireOp",EDGE,"E1.sketch_text.stroke-205"),sQuery(id+"F0.wireOp",EDGE,"E1.sketch_text.stroke-206"),sQuery(id+"F0.wireOp",EDGE,"E1.sketch_text.stroke-207"),sQuery(id+"F0.wireOp",EDGE,"E1.sketch_text.stroke-208"),sQuery(id+"F0.wireOp",EDGE,"E1.sketch_text.stroke-209"),sQuery(id+"F0.wireOp",EDGE,"E1.sketch_text.stroke-210"),sQuery(id+"F0.wireOp",EDGE,"E1.sketch_text.stroke-211"),sQuery(id+"F0.wireOp",EDGE,"E1.sketch_text.stroke-212"),sQuery(id+"F0.wireOp",EDGE,"E1.sketch_text.stroke-213"),sQuery(id+"F0.wireOp",EDGE,"E1.sketch_text.stroke-214"),sQuery(id+"F0.wireOp",EDGE,"E1.sketch_text.stroke-215"),sQuery(id+"F0.wireOp",EDGE,"E1.sketch_text.stroke-216"),sQuery(id+"F0.wireOp",EDGE,"E1.sketch_text.stroke-217"),sQuery(id+"F0.wireOp",EDGE,"E1.sketch_text.stroke-218"),sQuery(id+"F0.wireOp",EDGE,"E1.sketch_text.stroke-219"),sQuery(id+"F0.wireOp",EDGE,"E1.sketch_text.stroke-220"),sQuery(id+"F0.wireOp",EDGE,"E1.sketch_text.stroke-221"),sQuery(id+"F0.wireOp",EDGE,"E1.sketch_text.stroke-222"),sQuery(id+"F0.wireOp",EDGE,"E1.sketch_text.stroke-223"),sQuery(id+"F0.wireOp",EDGE,"E1.sketch_text.stroke-224"),sQuery(id+"F0.wireOp",EDGE,"E1.sketch_text.stroke-225"),sQuery(id+"F0.wireOp",EDGE,"E1.sketch_text.stroke-226"),sQuery(id+"F0.wireOp",EDGE,"E1.sketch_text.stroke-227"),sQuery(id+"F0.wireOp",EDGE,"E1.sketch_text.stroke-228"),sQuery(id+"F0.wireOp",EDGE,"E1.sketch_text.stroke-229"),sQuery(id+"F0.wireOp",EDGE,"E1.sketch_text.stroke-230"),sQuery(id+"F0.wireOp",EDGE,"E1.sketch_text.stroke-231"),sQuery(id+"F0.wireOp",EDGE,"E1.sketch_text.stroke-232"),sQuery(id+"F0.wireOp",EDGE,"E1.sketch_text.stroke-233"),sQuery(id+"F0.wireOp",EDGE,"E1.sketch_text.stroke-234"),sQuery(id+"F0.wireOp",EDGE,"E1.sketch_text.stroke-235"),sQuery(id+"F0.wireOp",EDGE,"E1.sketch_text.stroke-236"),sQuery(id+"F0.wireOp",EDGE,"E1.sketch_text.stroke-237"),sQuery(id+"F0.wireOp",EDGE,"E1.sketch_text.stroke-238"),sQuery(id+"F0.wireOp",EDGE,"E1.sketch_text.stroke-239"),sQuery(id+"F0.wireOp",EDGE,"E1.sketch_text.stroke-240"),sQuery(id+"F0.wireOp",EDGE,"E1.sketch_text.stroke-241"),sQuery(id+"F0.wireOp",EDGE,"E1.sketch_text.stroke-242"),sQuery(id+"F0.wireOp",EDGE,"E1.sketch_text.stroke-243"),sQuery(id+"F0.wireOp",EDGE,"E1.sketch_text.stroke-244"),sQuery(id+"F0.wireOp",EDGE,"E1.sketch_text.stroke-245"),sQuery(id+"F0.wireOp",EDGE,"E1.sketch_text.stroke-246"),sQuery(id+"F0.wireOp",EDGE,"E1.sketch_text.stroke-247"),sQuery(id+"F0.wireOp",EDGE,"E1.sketch_text.stroke-248"),sQuery(id+"F0.wireOp",EDGE,"E1.sketch_text.stroke-249"),sQuery(id+"F0.wireOp",EDGE,"E1.sketch_text.stroke-250"),sQuery(id+"F0.wireOp",EDGE,"E1.sketch_text.stroke-251"),sQuery(id+"F0.wireOp",EDGE,"E1.sketch_text.stroke-252"),sQuery(id+"F0.wireOp",EDGE,"E1.sketch_text.stroke-253"),sQuery(id+"F0.wireOp",EDGE,"E1.sketch_text.stroke-254"),sQuery(id+"F0.wireOp",EDGE,"E1.sketch_text.stroke-255"),sQuery(id+"F0.wireOp",EDGE,"E1.sketch_text.stroke-256"),sQuery(id+"F0.wireOp",EDGE,"E1.sketch_text.stroke-257"),sQuery(id+"F0.wireOp",EDGE,"E1.sketch_text.stroke-258"),sQuery(id+"F0.wireOp",EDGE,"E1.sketch_text.stroke-259"),sQuery(id+"F0.wireOp",EDGE,"E1.sketch_text.stroke-260"),sQuery(id+"F0.wireOp",EDGE,"E1.sketch_text.stroke-261"),sQuery(id+"F0.wireOp",EDGE,"E1.sketch_text.stroke-262"),sQuery(id+"F0.wireOp",EDGE,"E1.sketch_text.stroke-263"),sQuery(id+"F0.wireOp",EDGE,"E1.sketch_text.stroke-264"),sQuery(id+"F0.wireOp",EDGE,"E1.sketch_text.stroke-265"),sQuery(id+"F0.wireOp",EDGE,"E1.sketch_text.stroke-266"),sQuery(id+"F0.wireOp",EDGE,"E1.sketch_text.stroke-267"),sQuery(id+"F0.wireOp",EDGE,"E1.sketch_text.stroke-268"),sQuery(id+"F0.wireOp",EDGE,"E1.sketch_text.stroke-269"),sQuery(id+"F0.wireOp",EDGE,"E1.sketch_text.stroke-270"),sQuery(id+"F0.wireOp",EDGE,"E1.sketch_text.stroke-271"),sQuery(id+"F0.wireOp",EDGE,"E1.sketch_text.stroke-272"),sQuery(id+"F0.wireOp",EDGE,"E1.sketch_text.stroke-273"),sQuery(id+"F0.wireOp",EDGE,"E1.sketch_text.stroke-274"),sQuery(id+"F0.wireOp",EDGE,"E1.sketch_text.stroke-275"),sQuery(id+"F0.wireOp",EDGE,"E1.sketch_text.stroke-276"),sQuery(id+"F0.wireOp",EDGE,"E1.sketch_text.stroke-277"),sQuery(id+"F0.wireOp",EDGE,"E1.sketch_text.stroke-278"),sQuery(id+"F0.wireOp",EDGE,"E1.sketch_text.stroke-279"),sQuery(id+"F0.wireOp",EDGE,"E1.sketch_text.stroke-280"),sQuery(id+"F0.wireOp",EDGE,"E1.sketch_text.stroke-281"),sQuery(id+"F0.wireOp",EDGE,"E1.sketch_text.stroke-282"),sQuery(id+"F0.wireOp",EDGE,"E1.sketch_text.stroke-283"),sQuery(id+"F0.wireOp",EDGE,"E1.sketch_text.stroke-284"),sQuery(id+"F0.wireOp",EDGE,"E1.sketch_text.stroke-285"),sQuery(id+"F0.wireOp",EDGE,"E1.sketch_text.stroke-286"),sQuery(id+"F0.wireOp",EDGE,"E1.sketch_text.stroke-287"),sQuery(id+"F0.wireOp",EDGE,"E1.sketch_text.stroke-288"),sQuery(id+"F0.wireOp",EDGE,"E1.sketch_text.stroke-289"),sQuery(id+"F0.wireOp",EDGE,"E1.sketch_text.stroke-290"),sQuery(id+"F0.wireOp",EDGE,"E1.sketch_text.stroke-291"),sQuery(id+"F0.wireOp",EDGE,"E1.sketch_text.stroke-292"),sQuery(id+"F0.wireOp",EDGE,"E1.sketch_text.stroke-293"),sQuery(id+"F0.wireOp",EDGE,"E1.sketch_text.stroke-294"),sQuery(id+"F0.wireOp",EDGE,"E1.sketch_text.stroke-295"),sQuery(id+"F0.wireOp",EDGE,"E1.sketch_text.stroke-296"),sQuery(id+"F0.wireOp",EDGE,"E1.sketch_text.stroke-297"),sQuery(id+"F0.wireOp",EDGE,"E1.sketch_text.stroke-298"),sQuery(id+"F0.wireOp",EDGE,"E1.sketch_text.stroke-299"),sQuery(id+"F0.wireOp",EDGE,"E1.sketch_text.stroke-300"),sQuery(id+"F0.wireOp",EDGE,"E1.sketch_text.stroke-301"),sQuery(id+"F0.wireOp",EDGE,"E1.sketch_text.stroke-302"),sQuery(id+"F0.wireOp",EDGE,"E1.sketch_text.stroke-303"),sQuery(id+"F0.wireOp",EDGE,"E1.sketch_text.stroke-304"),sQuery(id+"F0.wireOp",EDGE,"E1.sketch_text.stroke-305"),sQuery(id+"F0.wireOp",EDGE,"E1.sketch_text.stroke-306"),sQuery(id+"F0.wireOp",EDGE,"E1.sketch_text.stroke-307"),sQuery(id+"F0.wireOp",EDGE,"E1.sketch_text.stroke-308"),sQuery(id+"F0.wireOp",EDGE,"E1.sketch_text.stroke-309"),sQuery(id+"F0.wireOp",EDGE,"E1.sketch_text.stroke-310"),sQuery(id+"F0.wireOp",EDGE,"E1.sketch_text.stroke-311"),sQuery(id+"F0.wireOp",EDGE,"E1.sketch_text.stroke-312"),sQuery(id+"F0.wireOp",EDGE,"E1.sketch_text.stroke-313"),sQuery(id+"F0.wireOp",EDGE,"E1.sketch_text.stroke-314"),sQuery(id+"F0.wireOp",EDGE,"E1.sketch_text.stroke-315"),sQuery(id+"F0.wireOp",EDGE,"E1.sketch_text.stroke-316"),sQuery(id+"F0.wireOp",EDGE,"E1.sketch_text.stroke-317"),sQuery(id+"F0.wireOp",EDGE,"E1.sketch_text.stroke-318"),sQuery(id+"F0.wireOp",EDGE,"E1.sketch_text.stroke-319"),sQuery(id+"F0.wireOp",EDGE,"E1.sketch_text.stroke-320"),sQuery(id+"F0.wireOp",EDGE,"E1.sketch_text.stroke-321"),sQuery(id+"F0.wireOp",EDGE,"E1.sketch_text.stroke-322"),sQuery(id+"F0.wireOp",EDGE,"E1.sketch_text.stroke-323"),sQuery(id+"F0.wireOp",EDGE,"E1.sketch_text.stroke-324"),sQuery(id+"F0.wireOp",EDGE,"E1.sketch_text.stroke-325"),sQuery(id+"F0.wireOp",EDGE,"E1.sketch_text.stroke-326"),sQuery(id+"F0.wireOp",EDGE,"E1.sketch_text.stroke-327"),sQuery(id+"F0.wireOp",EDGE,"E1.sketch_text.stroke-328"),sQuery(id+"F0.wireOp",EDGE,"E1.sketch_text.stroke-329"),sQuery(id+"F0.wireOp",EDGE,"E1.sketch_text.stroke-330"),sQuery(id+"F0.wireOp",EDGE,"E1.sketch_text.stroke-331"),sQuery(id+"F0.wireOp",EDGE,"E1.sketch_text.stroke-332"),sQuery(id+"F0.wireOp",EDGE,"E1.sketch_text.stroke-333"),sQuery(id+"F0.wireOp",EDGE,"E1.sketch_text.stroke-334"),sQuery(id+"F0.wireOp",EDGE,"E1.sketch_text.stroke-335"),sQuery(id+"F0.wireOp",EDGE,"E1.sketch_text.stroke-336"),sQuery(id+"F0.wireOp",EDGE,"E1.sketch_text.stroke-337"),sQuery(id+"F0.wireOp",EDGE,"E1.sketch_text.stroke-338"),sQuery(id+"F0.wireOp",EDGE,"E1.sketch_text.stroke-339"),sQuery(id+"F0.wireOp",EDGE,"E1.sketch_text.stroke-340"),sQuery(id+"F0.wireOp",EDGE,"E1.sketch_text.stroke-341"),sQuery(id+"F0.wireOp",EDGE,"E1.sketch_text.stroke-342"),sQuery(id+"F0.wireOp",EDGE,"E1.sketch_text.stroke-343"),sQuery(id+"F0.wireOp",EDGE,"E1.sketch_text.stroke-344"),sQuery(id+"F0.wireOp",EDGE,"E1.sketch_text.stroke-345"),sQuery(id+"F0.wireOp",EDGE,"E1.sketch_text.stroke-346"),sQuery(id+"F0.wireOp",EDGE,"E1.sketch_text.stroke-347"),sQuery(id+"F0.wireOp",EDGE,"E1.sketch_text.stroke-348"),sQuery(id+"F0.wireOp",EDGE,"E1.sketch_text.stroke-349"),sQuery(id+"F0.wireOp",EDGE,"E1.sketch_text.stroke-350"),sQuery(id+"F0.wireOp",EDGE,"E2.sketch_text.stroke-0"),sQuery(id+"F0.wireOp",EDGE,"E2.sketch_text.stroke-1"),sQuery(id+"F0.wireOp",EDGE,"E2.sketch_text.stroke-2"),sQuery(id+"F0.wireOp",EDGE,"E2.sketch_text.stroke-3"),sQuery(id+"F0.wireOp",EDGE,"E2.sketch_text.stroke-4"),sQuery(id+"F0.wireOp",EDGE,"E2.sketch_text.stroke-5"),sQuery(id+"F0.wireOp",EDGE,"E2.sketch_text.stroke-6"),sQuery(id+"F0.wireOp",EDGE,"E2.sketch_text.stroke-7"),sQuery(id+"F0.wireOp",EDGE,"E2.sketch_text.stroke-8"),sQuery(id+"F0.wireOp",EDGE,"E2.sketch_text.stroke-9"),sQuery(id+"F0.wireOp",EDGE,"E2.sketch_text.stroke-10"),sQuery(id+"F0.wireOp",EDGE,"E2.sketch_text.stroke-11"),sQuery(id+"F0.wireOp",EDGE,"E2.sketch_text.stroke-12"),sQuery(id+"F0.wireOp",EDGE,"E2.sketch_text.stroke-13"),sQuery(id+"F0.wireOp",EDGE,"E2.sketch_text.stroke-14"),sQuery(id+"F0.wireOp",EDGE,"E2.sketch_text.stroke-15"),sQuery(id+"F0.wireOp",EDGE,"E2.sketch_text.stroke-16"),sQuery(id+"F0.wireOp",EDGE,"E2.sketch_text.stroke-17"),sQuery(id+"F0.wireOp",EDGE,"E2.sketch_text.stroke-18"),sQuery(id+"F0.wireOp",EDGE,"E2.sketch_text.stroke-19"),sQuery(id+"F0.wireOp",EDGE,"E2.sketch_text.stroke-20"),sQuery(id+"F0.wireOp",EDGE,"E2.sketch_text.stroke-21"),sQuery(id+"F0.wireOp",EDGE,"E2.sketch_text.stroke-22"),sQuery(id+"F0.wireOp",EDGE,"E2.sketch_text.stroke-23"),sQuery(id+"F0.wireOp",EDGE,"E2.sketch_text.stroke-24"),sQuery(id+"F0.wireOp",EDGE,"E2.sketch_text.stroke-25"),sQuery(id+"F0.wireOp",EDGE,"E2.sketch_text.stroke-26"),sQuery(id+"F0.wireOp",EDGE,"E2.sketch_text.stroke-27"),sQuery(id+"F0.wireOp",EDGE,"E2.sketch_text.stroke-28"),sQuery(id+"F0.wireOp",EDGE,"E2.sketch_text.stroke-29"),sQuery(id+"F0.wireOp",EDGE,"E2.sketch_text.stroke-30"),sQuery(id+"F0.wireOp",EDGE,"E2.sketch_text.stroke-31"),sQuery(id+"F0.wireOp",EDGE,"E2.sketch_text.stroke-32"),sQuery(id+"F0.wireOp",EDGE,"E2.sketch_text.stroke-33"),sQuery(id+"F0.wireOp",EDGE,"E2.sketch_text.stroke-34"),sQuery(id+"F0.wireOp",EDGE,"E2.sketch_text.stroke-35"),sQuery(id+"F0.wireOp",EDGE,"E2.sketch_text.stroke-36"),sQuery(id+"F0.wireOp",EDGE,"E2.sketch_text.stroke-37"),sQuery(id+"F0.wireOp",EDGE,"E2.sketch_text.stroke-38"),sQuery(id+"F0.wireOp",EDGE,"E2.sketch_text.stroke-39"),sQuery(id+"F0.wireOp",EDGE,"E2.sketch_text.stroke-40"),sQuery(id+"F0.wireOp",EDGE,"E2.sketch_text.stroke-41"),sQuery(id+"F0.wireOp",EDGE,"E2.sketch_text.stroke-42"),sQuery(id+"F0.wireOp",EDGE,"E2.sketch_text.stroke-43"),sQuery(id+"F0.wireOp",EDGE,"E2.sketch_text.stroke-44"),sQuery(id+"F0.wireOp",EDGE,"E2.sketch_text.stroke-45"),sQuery(id+"F0.wireOp",EDGE,"E2.sketch_text.stroke-46"),sQuery(id+"F0.wireOp",EDGE,"E2.sketch_text.stroke-47"),sQuery(id+"F0.wireOp",EDGE,"E2.sketch_text.stroke-48"),sQuery(id+"F0.wireOp",EDGE,"E2.sketch_text.stroke-49"),sQuery(id+"F0.wireOp",EDGE,"E2.sketch_text.stroke-50"),sQuery(id+"F0.wireOp",EDGE,"E2.sketch_text.stroke-51"),sQuery(id+"F0.wireOp",EDGE,"E2.sketch_text.stroke-52"),sQuery(id+"F0.wireOp",EDGE,"E2.sketch_text.stroke-53"),sQuery(id+"F0.wireOp",EDGE,"E2.sketch_text.stroke-54"),sQuery(id+"F0.wireOp",EDGE,"E2.sketch_text.stroke-55"),sQuery(id+"F0.wireOp",EDGE,"E2.sketch_text.stroke-56"),sQuery(id+"F0.wireOp",EDGE,"E2.sketch_text.stroke-57"),sQuery(id+"F0.wireOp",EDGE,"E2.sketch_text.stroke-58"),sQuery(id+"F0.wireOp",EDGE,"E2.sketch_text.stroke-59"),sQuery(id+"F0.wireOp",EDGE,"E2.sketch_text.stroke-60"),sQuery(id+"F0.wireOp",EDGE,"E2.sketch_text.stroke-61"),sQuery(id+"F0.wireOp",EDGE,"E2.sketch_text.stroke-62"),sQuery(id+"F0.wireOp",EDGE,"E2.sketch_text.stroke-63"),sQuery(id+"F0.wireOp",EDGE,"E2.sketch_text.stroke-64"),sQuery(id+"F0.wireOp",EDGE,"E2.sketch_text.stroke-65"),sQuery(id+"F0.wireOp",EDGE,"E2.sketch_text.stroke-66"),sQuery(id+"F0.wireOp",EDGE,"E2.sketch_text.stroke-67"),sQuery(id+"F0.wireOp",EDGE,"E2.sketch_text.stroke-68"),sQuery(id+"F0.wireOp",EDGE,"E2.sketch_text.stroke-69"),sQuery(id+"F0.wireOp",EDGE,"E2.sketch_text.stroke-70"),sQuery(id+"F0.wireOp",EDGE,"E2.sketch_text.stroke-71"),sQuery(id+"F0.wireOp",EDGE,"E2.sketch_text.stroke-72"),sQuery(id+"F0.wireOp",EDGE,"E2.sketch_text.stroke-73"),sQuery(id+"F0.wireOp",EDGE,"E2.sketch_text.stroke-74"),sQuery(id+"F0.wireOp",EDGE,"E2.sketch_text.stroke-75"),sQuery(id+"F0.wireOp",EDGE,"E2.sketch_text.stroke-76"),sQuery(id+"F0.wireOp",EDGE,"E2.sketch_text.stroke-77"),sQuery(id+"F0.wireOp",EDGE,"E2.sketch_text.stroke-78"),sQuery(id+"F0.wireOp",EDGE,"E2.sketch_text.stroke-79"),sQuery(id+"F0.wireOp",EDGE,"E2.sketch_text.stroke-80"),sQuery(id+"F0.wireOp",EDGE,"E2.sketch_text.stroke-81"),sQuery(id+"F0.wireOp",EDGE,"E2.sketch_text.stroke-82"),sQuery(id+"F0.wireOp",EDGE,"E2.sketch_text.stroke-83"),sQuery(id+"F0.wireOp",EDGE,"E2.sketch_text.stroke-84"),sQuery(id+"F0.wireOp",EDGE,"E2.sketch_text.stroke-85"),sQuery(id+"F0.wireOp",EDGE,"E2.sketch_text.stroke-86"),sQuery(id+"F0.wireOp",EDGE,"E2.sketch_text.stroke-87"),sQuery(id+"F0.wireOp",EDGE,"E2.sketch_text.stroke-88"),sQuery(id+"F0.wireOp",EDGE,"E2.sketch_text.stroke-89"),sQuery(id+"F0.wireOp",EDGE,"E2.sketch_text.stroke-90"),sQuery(id+"F0.wireOp",EDGE,"E2.sketch_text.stroke-91"),sQuery(id+"F0.wireOp",EDGE,"E2.sketch_text.stroke-92"),sQuery(id+"F0.wireOp",EDGE,"E2.sketch_text.stroke-93"),sQuery(id+"F0.wireOp",EDGE,"E2.sketch_text.stroke-94"),sQuery(id+"F0.wireOp",EDGE,"E2.sketch_text.stroke-95"),sQuery(id+"F0.wireOp",EDGE,"E2.sketch_text.stroke-96"),sQuery(id+"F0.wireOp",EDGE,"E2.sketch_text.stroke-97"),sQuery(id+"F0.wireOp",EDGE,"E2.sketch_text.stroke-98"),sQuery(id+"F0.wireOp",EDGE,"E2.sketch_text.stroke-99"),sQuery(id+"F0.wireOp",EDGE,"E2.sketch_text.stroke-100"),sQuery(id+"F0.wireOp",EDGE,"E2.sketch_text.stroke-101"),sQuery(id+"F0.wireOp",EDGE,"E2.sketch_text.stroke-102"),sQuery(id+"F0.wireOp",EDGE,"E2.sketch_text.stroke-103"),sQuery(id+"F0.wireOp",EDGE,"E2.sketch_text.stroke-104"),sQuery(id+"F0.wireOp",EDGE,"E2.sketch_text.stroke-105"),sQuery(id+"F0.wireOp",EDGE,"E2.sketch_text.stroke-106"),sQuery(id+"F0.wireOp",EDGE,"E2.sketch_text.stroke-107"),sQuery(id+"F0.wireOp",EDGE,"E2.sketch_text.stroke-108"),sQuery(id+"F0.wireOp",EDGE,"E2.sketch_text.stroke-109"),sQuery(id+"F0.wireOp",EDGE,"E2.sketch_text.stroke-110"),sQuery(id+"F0.wireOp",EDGE,"E2.sketch_text.stroke-111"),sQuery(id+"F0.wireOp",EDGE,"E2.sketch_text.stroke-112"),sQuery(id+"F0.wireOp",EDGE,"E2.sketch_text.stroke-113"),sQuery(id+"F0.wireOp",EDGE,"E2.sketch_text.stroke-114"),sQuery(id+"F0.wireOp",EDGE,"E2.sketch_text.stroke-115"),sQuery(id+"F0.wireOp",EDGE,"E2.sketch_text.stroke-116"),sQuery(id+"F0.wireOp",EDGE,"E2.sketch_text.stroke-117"),sQuery(id+"F0.wireOp",EDGE,"E2.sketch_text.stroke-118"),sQuery(id+"F0.wireOp",EDGE,"E2.sketch_text.stroke-119"),sQuery(id+"F0.wireOp",EDGE,"E2.sketch_text.stroke-120"),sQuery(id+"F0.wireOp",EDGE,"E2.sketch_text.stroke-121"),sQuery(id+"F0.wireOp",EDGE,"E2.sketch_text.stroke-122"),sQuery(id+"F0.wireOp",EDGE,"E2.sketch_text.stroke-123"),sQuery(id+"F0.wireOp",EDGE,"E2.sketch_text.stroke-124"),sQuery(id+"F0.wireOp",EDGE,"E2.sketch_text.stroke-125"),sQuery(id+"F0.wireOp",EDGE,"E2.sketch_text.stroke-126"),sQuery(id+"F0.wireOp",EDGE,"E3"),sQuery(id+"F0.wireOp",EDGE,"E4"),subQ0,sQuery(id+"F0.wireOp",EDGE,"E6")])],"isStart":false})]});}
            fillet(context, id + "F3", {"entities" : qUnion([Q0]), "radius" : 1.27 * mm, "tangentPropagation" : true, "allowEdgeOverflow" : false});
        }
    });
